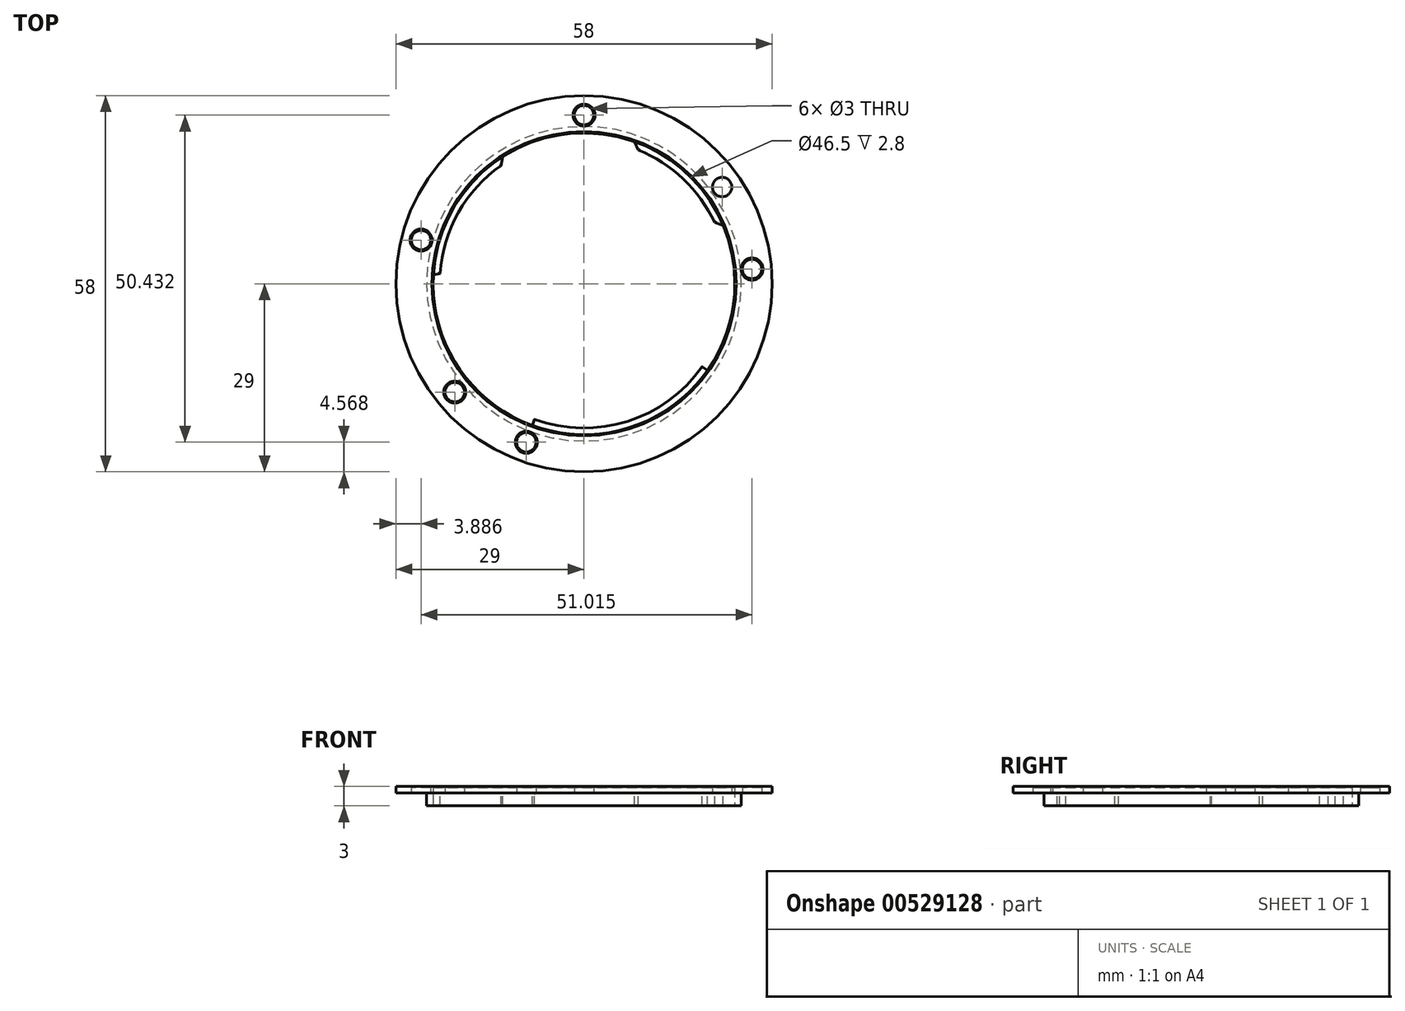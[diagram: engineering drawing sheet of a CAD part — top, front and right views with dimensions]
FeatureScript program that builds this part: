
annotation { "Feature Type Name" : "Feature", "Feature Type Description" : "" }
export const myFeature = defineFeature(function(context is Context, id is Id, definition is map)
    precondition{}
    {
        {
            var Q0;
            Q0=qCreatedBy(makeId("Top.planeOp"),FACE);
            var sketch = newSketch(context, id + "F0", { "sketchPlane" : qUnion([Q0])});
            skCircle(sketch, "E0", {"center": v(0, 0) * mm, "radius": 29 * mm});
            skCircle(sketch, "E1", {"center": v(0, 0) * mm, "radius": 23.25 * mm});
            skCircle(sketch, "E2", {"center": v(0, 0) * mm, "radius": 26 * mm, "construction": true});
            skCircle(sketch, "E3", {"center": v(0, 26) * mm, "radius": 1.5 * mm});
            skLineSegment(sketch, "E4", {"start": v(0, 0) * mm, "end": v(0, 35.64) * mm, "construction": true});
            skCircle(sketch, "E5", {"center": v(21.3, 14.91) * mm, "radius": 1.5 * mm});
            skLineSegment(sketch, "E6", {"start": v(21.3, 14.91) * mm, "end": v(0, 0) * mm, "construction": true});
            skLineSegment(sketch, "E7", {"start": v(0, 0) * mm, "end": v(25.9, 2.27) * mm, "construction": true});
            skLineSegment(sketch, "E8", {"start": v(0, 0) * mm, "end": v(-25.11, 6.73) * mm, "construction": true});
            skLineSegment(sketch, "E9", {"start": v(0, 0) * mm, "end": v(-19.92, -16.71) * mm, "construction": true});
            skLineSegment(sketch, "E10", {"start": v(0, 0) * mm, "end": v(-8.9, -24.43) * mm, "construction": true});
            skCircle(sketch, "E11", {"center": v(-25.11, 6.73) * mm, "radius": 1.5 * mm});
            skCircle(sketch, "E12", {"center": v(-19.92, -16.71) * mm, "radius": 1.5 * mm});
            skCircle(sketch, "E13", {"center": v(-8.9, -24.43) * mm, "radius": 1.5 * mm});
            skCircle(sketch, "E14", {"center": v(25.9, 2.27) * mm, "radius": 1.5 * mm});
            skSolve(sketch);
        }
        {
            var Q0;
            Q0=makeQuery(id+"F0.imprint","IMPRINT",FACE,{"disambiguationData":[TD([[makeQuery(id+"F0.imprint","IMPRINT",EDGE,{"derivedFrom":sQuery(id+"F0.wireOp",EDGE,"E0")}),1.0]])]});
            extrude(context, id + "F1", {"entities" : qUnion([Q0]), "depth" : 1 * mm, "offsetDistance" : 25 * mm});
        }
        {
            var Q0;
            Q0=makeQuery(id+"F1.opExtrude","CAP_FACE",FACE,{"disambiguationData":[OSD([sQuery(id+"F0.wireOp",EDGE,"E0"),sQuery(id+"F0.wireOp",EDGE,"E1"),sQuery(id+"F0.wireOp",EDGE,"E3"),sQuery(id+"F0.wireOp",EDGE,"E5"),sQuery(id+"F0.wireOp",EDGE,"E11"),sQuery(id+"F0.wireOp",EDGE,"E12"),sQuery(id+"F0.wireOp",EDGE,"E13"),sQuery(id+"F0.wireOp",EDGE,"E14")])],"isStart":true});
            var sketch = newSketch(context, id + "F2", { "sketchPlane" : qUnion([Q0])});
            skCircle(sketch, "E15.0.0", {"center": v(0, 0) * mm, "radius": 29 * mm});
            skCircle(sketch, "E16", {"center": v(0, 0) * mm, "radius": 22.25 * mm});
            skLineSegment(sketch, "E17", {"start": v(0, 0) * mm, "end": v(21.05, -9.87) * mm, "construction": true});
            skLineSegment(sketch, "E18", {"start": v(0, 0) * mm, "end": v(8.7, -21.56) * mm, "construction": true});
            skLineSegment(sketch, "E19", {"start": v(20.15, -9.44) * mm, "end": v(21.45, -8.97) * mm});
            skLineSegment(sketch, "E20", {"start": v(8.33, -20.63) * mm, "end": v(7.8, -21.9) * mm});
            skLineSegment(sketch, "E21", {"start": v(0, 0) * mm, "end": v(0, -32.43) * mm, "construction": true});
            skLineSegment(sketch, "E22", {"start": v(0, 0) * mm, "end": v(-23.2, -1.64) * mm, "construction": true});
            skLineSegment(sketch, "E23", {"start": v(0, 0) * mm, "end": v(-13.34, -19.05) * mm, "construction": true});
            skLineSegment(sketch, "E24", {"start": v(-12.76, -18.23) * mm, "end": v(-12.52, -19.6) * mm});
            skLineSegment(sketch, "E25", {"start": v(-22.2, -1.57) * mm, "end": v(-23.2, -1.38) * mm});
            skLineSegment(sketch, "E26", {"start": v(0, 0) * mm, "end": v(0, 32.49) * mm, "construction": true});
            skLineSegment(sketch, "E27", {"start": v(0, 0) * mm, "end": v(-7.95, 21.85) * mm, "construction": true});
            skLineSegment(sketch, "E28", {"start": v(0, 0) * mm, "end": v(19.05, 13.34) * mm, "construction": true});
            skLineSegment(sketch, "E29", {"start": v(-7.6, 20.9) * mm, "end": v(-7.95, 21.85) * mm});
            skLineSegment(sketch, "E30", {"start": v(18.23, 12.76) * mm, "end": v(19.05, 13.34) * mm});
            skCircle(sketch, "E31", {"center": v(0, 0) * mm, "radius": 24.25 * mm});
            skSolve(sketch);
        }
        {
            var Q0;
            {var subQ0=sQuery(id+"F2.wireOp",EDGE,"E19");Q0=makeQuery(id+"F2.imprint","IMPRINT",FACE,{"disambiguationData":[TD([[makeQuery(id+"F2.imprint","IMPRINT",EDGE,{"derivedFrom":subQ0}),-1.0]])]});}
            var Q1;
            {var subQ0=sQuery(id+"F2.wireOp",EDGE,"E24");Q1=makeQuery(id+"F2.imprint","IMPRINT",FACE,{"disambiguationData":[TD([[makeQuery(id+"F2.imprint","IMPRINT",EDGE,{"derivedFrom":subQ0}),-1.0]])]});}
            var Q2;
            {var subQ0=sQuery(id+"F2.wireOp",EDGE,"E29");Q2=makeQuery(id+"F2.imprint","IMPRINT",FACE,{"disambiguationData":[TD([[makeQuery(id+"F2.imprint","IMPRINT",EDGE,{"derivedFrom":subQ0}),-1.0]])]});}
            var Q3;
            Q3=makeQuery(id+"F2.imprint","IMPRINT",FACE,{"disambiguationData":[TD([[makeQuery(id+"F2.imprint","IMPRINT",EDGE,{"derivedFrom":sQuery(id+"F2.wireOp",EDGE,"E31")}),1.0]])]});
            extrude(context, id + "F3", {"entities" : qUnion([Q0, Q1, Q2, Q3]), "operationType" : NewBodyOperationType.ADD, "depth" : 2 * mm, "offsetDistance" : 25 * mm});
        }
        {
            var Q0;
            {var subQ0=sQuery(id+"F2.wireOp",EDGE,"E16");Q0=makeQuery(id+"F3.opExtrude","CAP_EDGE",EDGE,{"disambiguationData":[OSD([subQ0]),TDD([makeQuery(id+"F2.imprint","IMPRINT",EDGE,{"disambiguationData":[TD([[makeQuery(id+"F2.imprint","INTERSECT",VERTEX,{"derivedFrom":[subQ0,sQuery(id+"F2.wireOp",EDGE,"E19")]}),1.0]])],"derivedFrom":subQ0})])],"isStart":true});}
            var Q1;
            Q1=makeQuery(id+"F3.opExtrude","CAP_EDGE",EDGE,{"disambiguationData":[OSD([sQuery(id+"F2.wireOp",EDGE,"E20")])],"isStart":true});
            var Q2;
            {var subQ0=sQuery(id+"F2.wireOp",EDGE,"E16");Q2=makeQuery(id+"F3.opExtrude","CAP_EDGE",EDGE,{"disambiguationData":[OSD([subQ0]),TDD([makeQuery(id+"F2.imprint","IMPRINT",EDGE,{"disambiguationData":[TD([[makeQuery(id+"F2.imprint","INTERSECT",VERTEX,{"derivedFrom":[subQ0,sQuery(id+"F2.wireOp",EDGE,"E24")]}),1.0]])],"derivedFrom":subQ0})])],"isStart":true});}
            var Q3;
            Q3=makeQuery(id+"F3.opExtrude","CAP_EDGE",EDGE,{"disambiguationData":[OSD([sQuery(id+"F2.wireOp",EDGE,"E24")])],"isStart":true});
            var Q4;
            Q4=makeQuery(id+"F3.opExtrude","CAP_EDGE",EDGE,{"disambiguationData":[OSD([sQuery(id+"F2.wireOp",EDGE,"E19")])],"isStart":true});
            var Q5;
            Q5=makeQuery(id+"F3.opExtrude","CAP_EDGE",EDGE,{"disambiguationData":[OSD([sQuery(id+"F2.wireOp",EDGE,"E25")])],"isStart":true});
            var Q6;
            Q6=makeQuery(id+"F3.opExtrude","CAP_EDGE",EDGE,{"disambiguationData":[OSD([sQuery(id+"F2.wireOp",EDGE,"E30")])],"isStart":true});
            var Q7;
            Q7=makeQuery(id+"F3.opExtrude","CAP_EDGE",EDGE,{"disambiguationData":[OSD([sQuery(id+"F2.wireOp",EDGE,"E29")])],"isStart":true});
            var Q8;
            {var subQ0=sQuery(id+"F2.wireOp",EDGE,"E16");Q8=makeQuery(id+"F3.opExtrude","CAP_EDGE",EDGE,{"disambiguationData":[OSD([subQ0]),TDD([makeQuery(id+"F2.imprint","IMPRINT",EDGE,{"disambiguationData":[TD([[makeQuery(id+"F2.imprint","INTERSECT",VERTEX,{"derivedFrom":[subQ0,sQuery(id+"F2.wireOp",EDGE,"E29")]}),1.0]])],"derivedFrom":subQ0})])],"isStart":true});}
            fillet(context, id + "F4", {"entities" : qUnion([Q0, Q1, Q2, Q3, Q4, Q5, Q6, Q7, Q8]), "radius" : 0.2 * mm, "tangentPropagation" : true, "allowEdgeOverflow" : false});
        }
        {
            var Q0;
            Q0=makeQuery(id+"F1.opExtrude","CAP_EDGE",EDGE,{"disambiguationData":[OSD([sQuery(id+"F0.wireOp",EDGE,"E1")])],"isStart":false});
            var Q1;
            Q1=makeQuery(id+"F1.opExtrude","CAP_EDGE",EDGE,{"disambiguationData":[OSD([sQuery(id+"F0.wireOp",EDGE,"E14")])],"isStart":false});
            var Q2;
            Q2=makeQuery(id+"F1.opExtrude","CAP_EDGE",EDGE,{"disambiguationData":[OSD([sQuery(id+"F0.wireOp",EDGE,"E3")])],"isStart":false});
            var Q3;
            Q3=makeQuery(id+"F1.opExtrude","CAP_EDGE",EDGE,{"disambiguationData":[OSD([sQuery(id+"F0.wireOp",EDGE,"E12")])],"isStart":false});
            var Q4;
            Q4=makeQuery(id+"F1.opExtrude","CAP_EDGE",EDGE,{"disambiguationData":[OSD([sQuery(id+"F0.wireOp",EDGE,"E13")])],"isStart":false});
            var Q5;
            Q5=makeQuery(id+"F1.opExtrude","CAP_EDGE",EDGE,{"disambiguationData":[OSD([sQuery(id+"F0.wireOp",EDGE,"E11")])],"isStart":false});
            chamfer(context, id + "F5", {"entities" : qUnion([Q0, Q1, Q2, Q3, Q4, Q5]), "width" : 0.2 * mm, "tangentPropagation" : true});
        }
    });
